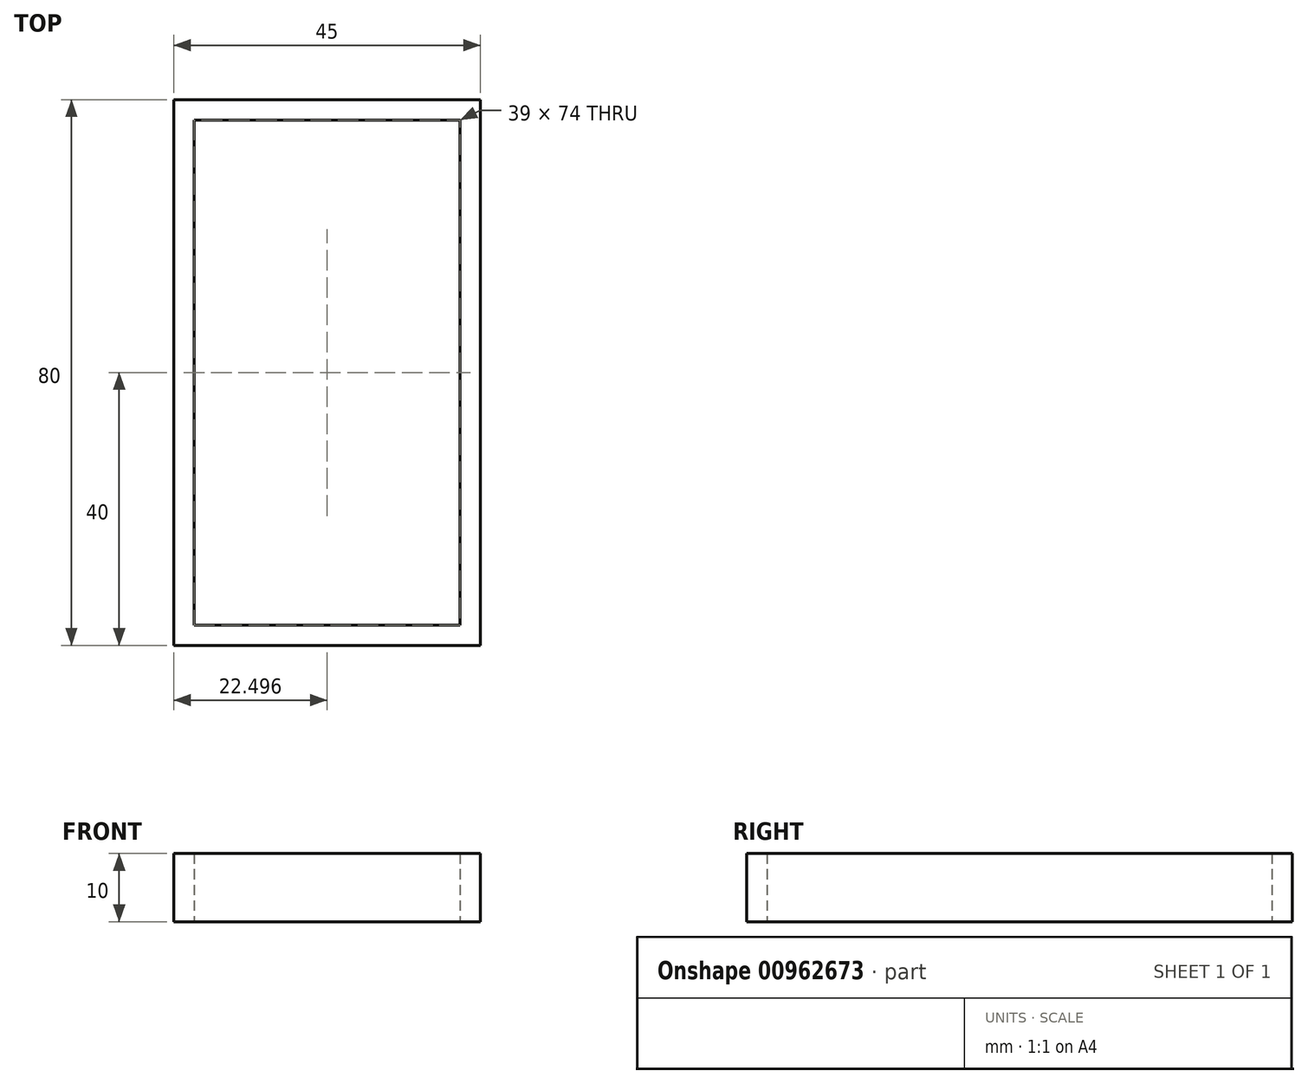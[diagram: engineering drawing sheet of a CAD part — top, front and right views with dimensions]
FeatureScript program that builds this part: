
annotation { "Feature Type Name" : "Feature", "Feature Type Description" : "" }
export const myFeature = defineFeature(function(context is Context, id is Id, definition is map)
    precondition{}
    {
        {
            var Q0;
            Q0=qCreatedBy(makeId("Top.planeOp"),FACE);
            var sketch = newSketch(context, id + "F0", { "sketchPlane" : qUnion([Q0])});
            skLineSegment(sketch, "E0.bottom", {"start": v(-226.8, 33.8) * mm, "end": v(-181.8, 33.8) * mm});
            skLineSegment(sketch, "E0.top", {"start": v(-226.8, -46.2) * mm, "end": v(-181.8, -46.2) * mm});
            skLineSegment(sketch, "E0.left", {"start": v(-226.8, 33.8) * mm, "end": v(-226.8, -46.2) * mm});
            skLineSegment(sketch, "E0.right", {"start": v(-181.8, 33.8) * mm, "end": v(-181.8, -46.2) * mm});
            skLineSegment(sketch, "E1.bottom", {"start": v(-223.8, 30.8) * mm, "end": v(-184.8, 30.8) * mm});
            skLineSegment(sketch, "E1.top", {"start": v(-223.8, -43.2) * mm, "end": v(-184.8, -43.2) * mm});
            skLineSegment(sketch, "E1.left", {"start": v(-223.8, 30.8) * mm, "end": v(-223.8, -43.2) * mm});
            skLineSegment(sketch, "E1.right", {"start": v(-184.8, 30.8) * mm, "end": v(-184.8, -43.2) * mm});
            skSolve(sketch);
        }
        {
            var Q0;
            Q0=makeQuery(id+"F0.imprint","IMPRINT",FACE,{"disambiguationData":[TD([[makeQuery(id+"F0.imprint","IMPRINT",EDGE,{"derivedFrom":sQuery(id+"F0.wireOp",EDGE,"E0.bottom")}),-1.0]])]});
            extrude(context, id + "F1", {"entities" : qUnion([Q0]), "depth" : 10 * mm, "offsetDistance" : 25 * mm});
        }
    });
